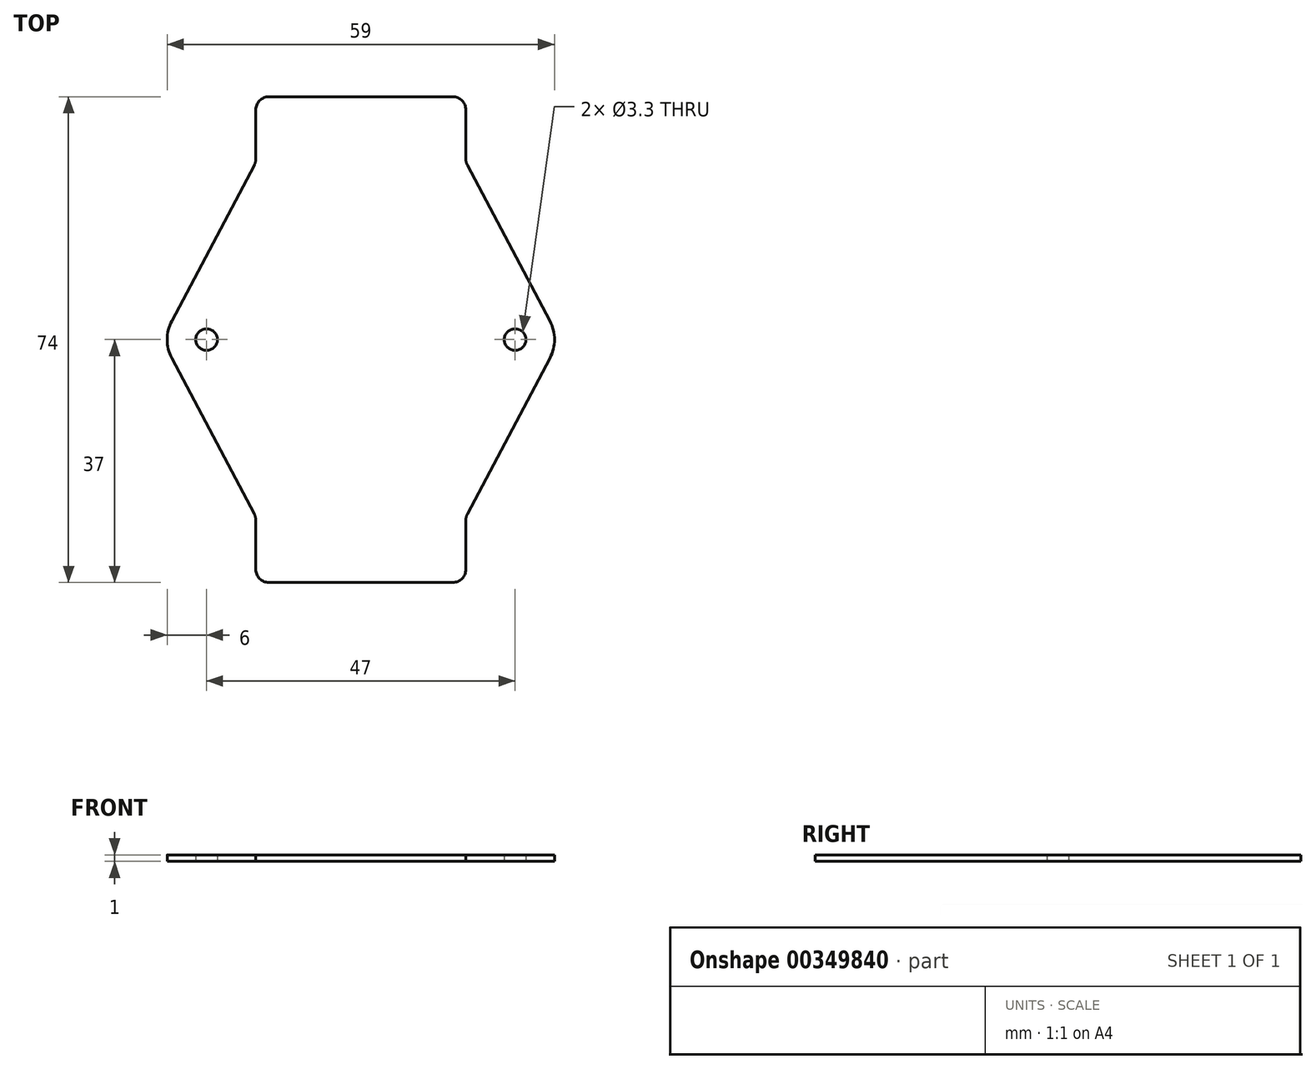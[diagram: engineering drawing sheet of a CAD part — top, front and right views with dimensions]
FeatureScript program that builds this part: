
annotation { "Feature Type Name" : "Feature", "Feature Type Description" : "" }
export const myFeature = defineFeature(function(context is Context, id is Id, definition is map)
    precondition{}
    {
        {
            var Q0;
            Q0=qCreatedBy(makeId("Top.planeOp"),FACE);
            var sketch = newSketch(context, id + "F0", { "sketchPlane" : qUnion([Q0])});
            skLineSegment(sketch, "E0.bottom", {"start": v(0, 0) * mm, "end": v(14, 0) * mm});
            skLineSegment(sketch, "E0.top", {"start": v(0, 74) * mm, "end": v(14, 74) * mm});
            skLineSegment(sketch, "E0.left", {"start": v(0, 0) * mm, "end": v(0, 74) * mm});
            skLineSegment(sketch, "E0.right", {"start": v(16, 2) * mm, "end": v(16, 9.5) * mm});
            skArc(sketch, "E1", {"start": v(28.8, 34.2) * mm, "mid": v(29.5, 37) * mm, "end": v(28.8, 39.8) * mm});
            skLineSegment(sketch, "E2", {"start": v(28.8, 34.2) * mm, "end": v(16.23, 10.44) * mm});
            skLineSegment(sketch, "E3", {"start": v(28.8, 39.8) * mm, "end": v(16.23, 63.56) * mm});
            skLineSegment(sketch, "E4.trimOffspring", {"start": v(16, 64.5) * mm, "end": v(16, 72) * mm});
            skCircle(sketch, "E5", {"center": v(23.5, 37) * mm, "radius": 1.65 * mm});
            skPoint(sketch, "E6.visualSharp", {"position": v(16, 74) * mm});
            skArc(sketch, "E6.filletArc", {"start": v(16, 72) * mm, "mid": v(15.41, 73.41) * mm, "end": v(14, 74) * mm});
            skPoint(sketch, "E7.visualSharp", {"position": v(16, 0) * mm});
            skArc(sketch, "E7.filletArc", {"start": v(14, 0) * mm, "mid": v(15.41, 0.59) * mm, "end": v(16, 2) * mm});
            skPoint(sketch, "E8.visualSharp", {"position": v(16, 10) * mm});
            skArc(sketch, "E8.filletArc", {"start": v(16.23, 10.44) * mm, "mid": v(16.06, 9.99) * mm, "end": v(16, 9.5) * mm});
            skPoint(sketch, "E9.visualSharp", {"position": v(16, 64) * mm});
            skArc(sketch, "E9.filletArc", {"start": v(16, 64.5) * mm, "mid": v(16.06, 64.01) * mm, "end": v(16.23, 63.56) * mm});
            skArc(sketch, "E10.MirrorCS", {"start": v(-16.23, 10.44) * mm, "mid": v(-16.06, 9.99) * mm, "end": v(-16, 9.5) * mm});
            skArc(sketch, "E11.MirrorCS", {"start": v(-16, 64.5) * mm, "mid": v(-16.06, 64.01) * mm, "end": v(-16.23, 63.56) * mm});
            skArc(sketch, "E12.MirrorCS", {"start": v(-16, 72) * mm, "mid": v(-15.41, 73.41) * mm, "end": v(-14, 74) * mm});
            skArc(sketch, "E13.MirrorCS", {"start": v(-14, 0) * mm, "mid": v(-15.41, 0.59) * mm, "end": v(-16, 2) * mm});
            skCircle(sketch, "E14.MirrorC", {"center": v(-23.5, 37) * mm, "radius": 1.65 * mm});
            skLineSegment(sketch, "E15.MirrorCS", {"start": v(-16, 64.5) * mm, "end": v(-16, 72) * mm});
            skLineSegment(sketch, "E16.MirrorCS", {"start": v(-28.8, 39.8) * mm, "end": v(-16.23, 63.56) * mm});
            skPoint(sketch, "E17.MirrorP", {"position": v(-16, 64) * mm});
            skLineSegment(sketch, "E18.MirrorCS", {"start": v(-28.8, 34.2) * mm, "end": v(-16.23, 10.44) * mm});
            skArc(sketch, "E19.MirrorCS", {"start": v(-28.8, 34.2) * mm, "mid": v(-29.5, 37) * mm, "end": v(-28.8, 39.8) * mm});
            skLineSegment(sketch, "E20.MirrorCS", {"start": v(-16, 2) * mm, "end": v(-16, 9.5) * mm});
            skPoint(sketch, "E21.MirrorP", {"position": v(-16, 74) * mm});
            skLineSegment(sketch, "E22.MirrorCS", {"start": v(0, 74) * mm, "end": v(-14, 74) * mm});
            skLineSegment(sketch, "E23.MirrorCS", {"start": v(0, 0) * mm, "end": v(-14, 0) * mm});
            skPoint(sketch, "E24.MirrorP", {"position": v(-16, 0) * mm});
            skPoint(sketch, "E25.MirrorP", {"position": v(-16, 10) * mm});
            skSolve(sketch);
        }
        {
            var Q0;
            Q0 = qSketchRegion(id + "F0", true);
            extrude(context, id + "F1", {"entities" : qUnion([Q0]), "depth" : 1 * mm});
        }
    });
